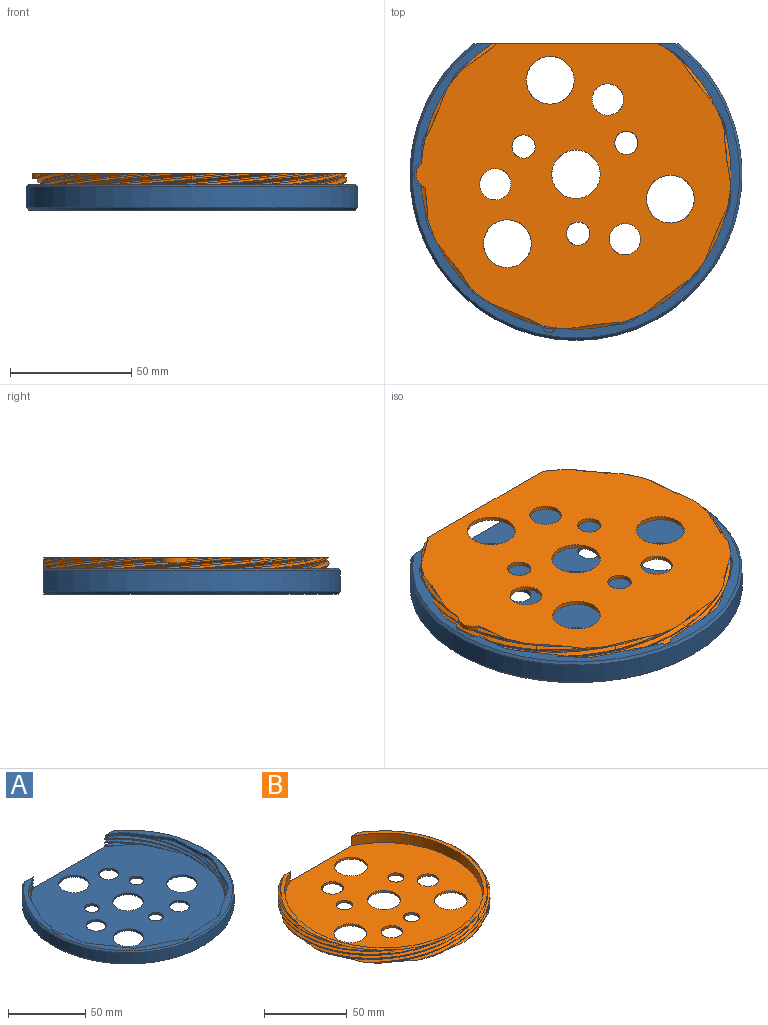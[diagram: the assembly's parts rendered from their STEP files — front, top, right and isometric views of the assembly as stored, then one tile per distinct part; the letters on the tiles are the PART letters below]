
ASSEMBLY  parts=2 mates=1
PART A: 110 faces, bbox 137.5x125.1x13.2 mm
  f0: cylinder r=63.1mm len=7.96mm, axis (0,0,1), area 4.3mm2, adj f1,f2,f33,f59
  f1: plane 128.57x118.32mm, normal (0,0,1), area 10495.3mm2, adj f0,f2,f3,f12,f13,f14,f15,f16
  f2: plane 84.9x10.88mm, normal (0,1,0), area 288.5mm2, adj f0,f1,f4,f5,f6,f7,f8,f9
  f3: cylinder r=10mm len=20mm, axis (0,0,-1), area 100.5mm2, adj f1,f5
  f4: cylinder r=68.6mm len=137.2mm, axis (0,0,-1), area 2922.7mm2, adj f2,f95,f96
  f5: plane 135.2x121.6mm, normal (0,0,-1), area 11755.3mm2, adj f2,f3,f95,f101,f102,f103,f104,f105
  f6: bspline ~56.05x33.17mm, area 111.1mm2, adj f2,f8,f61,f88,f98
  f7: bspline ~56.05x33.17mm, area 83.7mm2, adj f2,f8,f60,f90
  f8: bspline ~56.17x32.5mm, area 22.3mm2, adj f2,f6,f7,f89
  f9: bspline ~56.05x33.17mm, area 48.2mm2, adj f2,f11,f60,f91
  f10: bspline ~24.5x24.5mm, area 20.8mm2, adj f2,f11,f58,f93
  f11: bspline ~23.81x23.81mm, area 7.5mm2, adj f2,f9,f10,f92
  f12: bspline ~88.41x33.17mm, area 146.2mm2, adj f1,f14,f62,f63,f84
  f13: bspline ~88.41x33.17mm, area 146.8mm2, adj f1,f14,f42,f82
  f14: bspline ~88.6x32.5mm, area 34.4mm2, adj f1,f12,f13,f83
  f15: bspline ~88.41x33.17mm, area 144.9mm2, adj f1,f2,f17,f61,f87
  f16: bspline ~88.41x33.17mm, area 146.8mm2, adj f1,f17,f62,f85
  f17: bspline ~88.6x32.5mm, area 34.4mm2, adj f1,f15,f16,f86
  f18: bspline ~88.41x33.17mm, area 146.2mm2, adj f1,f20,f46,f47,f75
  f19: bspline ~88.41x33.17mm, area 146.8mm2, adj f1,f20,f48,f73
  f20: bspline ~88.6x32.5mm, area 34.4mm2, adj f1,f18,f19,f74
  f21: bspline ~64.72x64.72mm, area 146.2mm2, adj f1,f23,f48,f49,f72
  f22: bspline ~64.72x64.72mm, area 146.8mm2, adj f1,f23,f50,f70
  f23: bspline ~64.86x64.86mm, area 34.4mm2, adj f1,f21,f22,f71
  f24: bspline ~64.72x64.72mm, area 146.2mm2, adj f1,f26,f42,f43,f81
  f25: bspline ~64.72x64.72mm, area 146.8mm2, adj f1,f26,f44,f79,f100
  f26: bspline ~64.86x64.86mm, area 34.4mm2, adj f1,f24,f25,f80,f100
  f27: bspline ~74.82x33.17mm, area 146.2mm2, adj f1,f29,f44,f45,f78
  f28: bspline ~88.41x33.17mm, area 146.8mm2, adj f1,f29,f46,f76
  f29: bspline ~88.6x32.5mm, area 34.4mm2, adj f1,f27,f28,f77
  f30: bspline ~56.05x33.17mm, area 89mm2, adj f1,f2,f32,f56
  f31: bspline ~56.05x33.17mm, area 115.7mm2, adj f1,f2,f32,f54,f55
  f32: bspline ~56.17x32.5mm, area 23.5mm2, adj f1,f2,f30,f31
  f33: bspline ~24.5x24.5mm, area 26mm2, adj f0,f1,f2,f35
  f34: bspline ~23.84x23.41mm, area 52.7mm2, adj f1,f2,f35,f56,f57
  f35: bspline ~23.81x23.81mm, area 8.7mm2, adj f1,f2,f33,f34
  f36: bspline ~74.82x33.17mm, area 146.2mm2, adj f1,f38,f50,f51,f69
  f37: bspline ~88.41x33.17mm, area 146.8mm2, adj f1,f38,f52,f67
  f38: bspline ~88.6x32.5mm, area 34.4mm2, adj f1,f36,f37,f68
  f39: bspline ~88.41x33.17mm, area 146.2mm2, adj f1,f41,f52,f53,f66
  f40: bspline ~88.41x33.17mm, area 146.6mm2, adj f1,f2,f41,f54,f64
  f41: bspline ~88.6x32.5mm, area 34.4mm2, adj f1,f39,f40,f65
  f42: cylinder r=63.1mm len=69.34mm, axis (0,0,1), area 75mm2, adj f1,f13,f24,f43,f81,f82,f94
  f43: bspline ~10.54x2.52mm, area 0.5mm2, adj f1,f24,f42
  f44: cylinder r=63.1mm len=67.62mm, axis (0,0,1), area 75mm2, adj f1,f25,f27,f45,f78,f79,f94
  f45: bspline ~10.16x5.89mm, area 0.5mm2, adj f1,f27,f44
  f46: cylinder r=63.1mm len=79.07mm, axis (0,0,1), area 75mm2, adj f1,f18,f28,f47,f75,f76,f94
  f47: bspline ~9.49x7.32mm, area 0.5mm2, adj f1,f18,f46
  f48: cylinder r=63.1mm len=69.34mm, axis (0,0,1), area 75mm2, adj f1,f19,f21,f49,f72,f73,f94
  f49: bspline ~10.54x2.52mm, area 0.5mm2, adj f1,f21,f48
  f50: cylinder r=63.1mm len=67.62mm, axis (0,0,1), area 75mm2, adj f1,f22,f36,f51,f69,f70,f94
  f51: bspline ~10.16x5.89mm, area 0.5mm2, adj f1,f36,f50
  f52: cylinder r=63.1mm len=79.07mm, axis (0,0,1), area 75mm2, adj f1,f37,f39,f53,f66,f67,f94
  f53: bspline ~9.49x7.32mm, area 0.5mm2, adj f1,f39,f52
  f54: cylinder r=63.1mm len=65.01mm, axis (0,0,1), area 54.1mm2, adj f1,f2,f31,f40,f55
  f55: bspline ~10.54x2.52mm, area 0.5mm2, adj f1,f31,f54
  f56: cylinder r=63.1mm len=32.47mm, axis (0,0,1), area 29.2mm2, adj f1,f2,f30,f34,f57
  f57: bspline ~10.16x5.89mm, area 0.5mm2, adj f1,f34,f56
  f58: cylinder r=63.1mm len=5.83mm, axis (0,0,1), area 16.4mm2, adj f2,f10,f93,f94
  f59: bspline ~9.49x7.32mm, area 0.1mm2, adj f0,f1,f2
  f60: cylinder r=63.1mm len=29.92mm, axis (0,0,1), area 43.7mm2, adj f2,f7,f9,f90,f91,f94
  f61: cylinder r=63.1mm len=62.31mm, axis (0,0,1), area 55.7mm2, adj f2,f6,f15,f87,f94,f97,f98
  f62: cylinder r=63.1mm len=79.07mm, axis (0,0,1), area 75mm2, adj f1,f12,f16,f63,f84,f85,f94
  f63: bspline ~9.49x7.32mm, area 0.5mm2, adj f1,f12,f62
  f64: extruded ~7.96x4.01mm, area 17.8mm2, adj f2,f40,f65,f94
  f65: extruded ~3.15x2.77mm, area 8.4mm2, adj f41,f64,f66,f94
  f66: extruded ~8.75x5.76mm, area 21mm2, adj f39,f52,f65,f94
  f67: extruded ~8.81x5.95mm, area 21.3mm2, adj f37,f52,f68,f94
  f68: extruded ~3.98x2mm, area 8.4mm2, adj f38,f67,f69,f94
  f69: extruded ~10.46x2mm, area 21mm2, adj f36,f50,f68,f94
  f70: extruded ~10.61x2mm, area 21.3mm2, adj f22,f50,f71,f94
  f71: extruded ~4.12x2mm, area 8.4mm2, adj f23,f70,f72,f94
  f72: extruded ~9.36x4.7mm, area 21mm2, adj f21,f48,f71,f94
  f73: extruded ~9.56x4.65mm, area 21.3mm2, adj f19,f48,f74,f94
  f74: extruded ~3.15x2.77mm, area 8.4mm2, adj f20,f73,f75,f94
  f75: extruded ~8.75x5.76mm, area 21mm2, adj f18,f46,f74,f94
  f76: extruded ~8.81x5.95mm, area 21.3mm2, adj f28,f46,f77,f94
  f77: extruded ~3.98x2mm, area 8.4mm2, adj f29,f76,f78,f94
  f78: extruded ~10.46x2mm, area 21mm2, adj f27,f44,f77,f94
  f79: extruded ~8.75x2mm, area 17.6mm2, adj f25,f44,f94,f99
  f80: extruded ~2x1.13mm, area 2.4mm2, adj f26,f81,f94,f99
  f81: extruded ~9.36x4.7mm, area 21mm2, adj f24,f42,f80,f94
  f82: extruded ~9.56x4.65mm, area 21.3mm2, adj f13,f42,f83,f94
  f83: extruded ~3.15x2.77mm, area 8.4mm2, adj f14,f82,f84,f94
  f84: extruded ~8.75x5.76mm, area 21mm2, adj f12,f62,f83,f94
  f85: extruded ~8.81x5.95mm, area 21.3mm2, adj f16,f62,f86,f94
  f86: extruded ~3.98x2mm, area 8.4mm2, adj f17,f85,f87,f94
  f87: extruded ~10.46x2mm, area 21mm2, adj f15,f61,f86,f94
  f88: extruded ~4.68x2mm, area 9.4mm2, adj f6,f89,f94,f97
  f89: extruded ~4.12x2mm, area 8.4mm2, adj f8,f88,f90,f94
  f90: extruded ~9.36x4.7mm, area 21mm2, adj f7,f60,f89,f94
  f91: extruded ~9.56x4.65mm, area 21.3mm2, adj f9,f60,f92,f94
  f92: extruded ~3.15x2.77mm, area 8.4mm2, adj f11,f91,f93,f94
  f93: extruded ~8.75x5.76mm, area 21mm2, adj f10,f58,f92,f94
  f94: plane 135.29x121.69mm, normal (0,0,1), area 1215.9mm2, adj f2,f42,f44,f46,f48,f50,f52,f58
  f95: cone r=68.6mm half-angle=45deg, axis (0,0,1), area 478.9mm2, adj f2,f4,f5
  f96: cone r=67.6mm half-angle=45deg, axis (0,0,-1), area 478.9mm2, adj f2,f4,f94
  f97: cylinder r=7mm len=12.35mm, axis (0,0,1), area 30.4mm2, adj f61,f88,f94,f98
  f98: plane 12.38x4.26mm, normal (0,0,1), area 33.4mm2, adj f6,f61,f97
  f99: cylinder r=2.5mm len=4.84mm, axis (0,0,1), area 13.4mm2, adj f79,f80,f94,f100
  f100: plane 4.99x2.32mm, normal (0,0,1), area 6.3mm2, adj f25,f26,f99
  f101: cylinder r=4.81mm len=9.61mm, axis (0,0,-1), area 48.3mm2, adj f1,f5
  f102: cylinder r=9.88mm len=19.75mm, axis (0,0,-1), area 99.3mm2, adj f1,f5
  f103: cylinder r=6.48mm len=12.97mm, axis (0,0,-1), area 65.2mm2, adj f1,f5
  f104: cylinder r=4.81mm len=9.61mm, axis (0,0,-1), area 48.3mm2, adj f1,f5
  f105: cylinder r=9.88mm len=19.75mm, axis (0,0,-1), area 99.3mm2, adj f1,f5
  f106: cylinder r=6.48mm len=12.97mm, axis (0,0,-1), area 65.2mm2, adj f1,f5
  f107: cylinder r=4.81mm len=9.61mm, axis (0,0,-1), area 48.3mm2, adj f1,f5
  f108: cylinder r=9.88mm len=19.75mm, axis (0,0,-1), area 99.3mm2, adj f1,f5
  f109: cylinder r=6.48mm len=12.97mm, axis (0,0,-1), area 65.2mm2, adj f1,f5
PART B: 109 faces, bbox 130.1x126.5x14.6 mm
  f0: bspline ~10.5x1.88mm, area 0.4mm2, adj f1,f76,f98
  f1: cylinder r=64mm len=77.53mm, axis (0,0,-1), area 36.1mm2, adj f0,f16,f65,f76,f78,f87,f98,f99
  f2: cylinder r=64mm len=75.65mm, axis (0,0,-1), area 36.5mm2, adj f16,f62,f66,f69,f88
  f3: cylinder r=64mm len=75.65mm, axis (0,0,-1), area 36.5mm2, adj f16,f35,f39,f56,f91
  f4: cylinder r=64mm len=58.63mm, axis (0,0,-1), area 36.5mm2, adj f16,f50,f53,f57,f90
  f5: cylinder r=64mm len=58.63mm, axis (0,0,-1), area 36.5mm2, adj f16,f44,f59,f63,f89
  f6: cylinder r=64mm len=77.53mm, axis (0,0,-1), area 36.5mm2, adj f16,f38,f41,f45,f93
  f7: cylinder r=64mm len=75.65mm, axis (0,0,-1), area 36.5mm2, adj f16,f25,f29,f32,f95
  f8: cylinder r=64mm len=77.53mm, axis (0,0,-1), area 36.5mm2, adj f16,f28,f47,f51,f92
  f9: cylinder r=64mm len=15.18mm, axis (0,0,-1), area 6.8mm2, adj f15,f20,f24,f96
  f10: cylinder r=64mm len=43.66mm, axis (0,0,-1), area 19.4mm2, adj f15,f19,f33,f94
  f11: cylinder r=64mm len=18.67mm, axis (0,0,-1), area 15.1mm2, adj f15,f16,f73,f81
  f12: cylinder r=64mm len=49.38mm, axis (0,0,-1), area 27.8mm2, adj f15,f16,f75,f82,f84,f99
  f13: plane 120x114mm, normal (0,0,1), area 9250.9mm2, adj f14,f15,f17,f100,f101,f102,f103,f104
  f14: cylinder r=10mm len=20mm, axis (0,0,-1), area 100.5mm2, adj f13,f16
  f15: plane 68.75x8.65mm, normal (0,1,0), area 190.4mm2, adj f9,f10,f11,f12,f13,f16,f17,f18
  f16: plane 129.9x117.9mm, normal (0,0,-1), area 10370.3mm2, adj f1,f2,f3,f4,f5,f6,f7,f8
  f17: cylinder r=60mm len=120mm, axis (0,0,-1), area 2260.1mm2, adj f13,f15,f18
  f18: plane 125.06x116.56mm, normal (0,0,1), area 791.7mm2, adj f15,f17,f19,f20,f21,f22,f23,f24
  f19: bspline ~55.43x32.81mm, area 99.6mm2, adj f10,f15,f18,f21,f94
  f20: bspline ~55.43x32.81mm, area 64.5mm2, adj f9,f15,f18,f21,f96
  f21: bspline ~62.38x62.38mm, area 43mm2, adj f15,f18,f19,f20
  f22: bspline ~54.02x31.3mm, area 15.5mm2, adj f15,f18,f23,f24
  f23: bspline ~24.24x24.24mm, area 7.9mm2, adj f15,f18,f22,f97
  f24: bspline ~24.24x24.24mm, area 37.4mm2, adj f9,f15,f18,f22,f96
  f25: bspline ~25.28x22.34mm, area 24.3mm2, adj f7,f16,f27,f29
  f26: bspline ~25.28x22.34mm, area 3.2mm2, adj f16,f27,f28
  f27: bspline ~23.99x21.05mm, area 8.4mm2, adj f16,f25,f26,f30
  f28: bspline ~81.93x24.95mm, area 162.6mm2, adj f8,f16,f18,f26,f30,f92
  f29: bspline ~75.77x18.47mm, area 129.4mm2, adj f7,f18,f25,f30,f95
  f30: bspline ~79.37x22.84mm, area 70.3mm2, adj f18,f27,f28,f29
  f31: bspline ~0.73x0.26mm, area 0.1mm2, adj f15,f34
  f32: bspline ~87.43x32.81mm, area 161.4mm2, adj f7,f15,f16,f18,f34,f95
  f33: bspline ~87.43x32.81mm, area 126.8mm2, adj f10,f15,f18,f34,f94
  f34: bspline ~85.21x31.3mm, area 70.3mm2, adj f15,f18,f31,f32,f33
  f35: bspline ~25.28x22.34mm, area 24.3mm2, adj f3,f16,f37,f39
  f36: bspline ~25.28x22.34mm, area 3.2mm2, adj f16,f37,f38
  f37: bspline ~23.99x21.05mm, area 8.4mm2, adj f16,f35,f36,f40
  f38: bspline ~81.93x24.95mm, area 162.6mm2, adj f6,f16,f18,f36,f40,f93
  f39: bspline ~75.77x18.47mm, area 129.4mm2, adj f3,f18,f35,f40,f91
  f40: bspline ~79.37x22.84mm, area 70.3mm2, adj f18,f37,f38,f39
  f41: bspline ~31.93x7.88mm, area 24.3mm2, adj f6,f16,f43,f45
  f42: bspline ~31.94x7.88mm, area 3.2mm2, adj f16,f43,f44
  f43: bspline ~31.14x6.46mm, area 8.4mm2, adj f16,f41,f42,f46
  f44: bspline ~64x64mm, area 162.6mm2, adj f5,f16,f18,f42,f46,f89
  f45: bspline ~64x64mm, area 129.4mm2, adj f6,f18,f41,f46,f93
  f46: bspline ~62.38x62.38mm, area 70.3mm2, adj f18,f43,f44,f45
  f47: bspline ~31.93x7.88mm, area 24.3mm2, adj f8,f16,f49,f51
  f48: bspline ~31.94x7.88mm, area 3.2mm2, adj f16,f49,f50
  f49: bspline ~31.14x6.46mm, area 8.4mm2, adj f16,f47,f48,f52
  f50: bspline ~64x64mm, area 162.6mm2, adj f4,f16,f18,f48,f52,f90
  f51: bspline ~64x64mm, area 129.4mm2, adj f8,f18,f47,f52,f92
  f52: bspline ~62.38x62.38mm, area 70.3mm2, adj f18,f49,f50,f51
  f53: bspline ~18.07x9.25mm, area 24.3mm2, adj f4,f16,f55,f57
  f54: bspline ~5.55x3.77mm, area 3.2mm2, adj f16,f55,f56
  f55: bspline ~12.68x6.34mm, area 8.4mm2, adj f16,f53,f54,f58
  f56: bspline ~87.43x32.81mm, area 162.6mm2, adj f3,f16,f18,f54,f58,f91
  f57: bspline ~87.43x32.81mm, area 129.4mm2, adj f4,f18,f53,f58,f90
  f58: bspline ~85.21x31.3mm, area 70.3mm2, adj f18,f55,f56,f57
  f59: bspline ~18.07x9.25mm, area 24.3mm2, adj f5,f16,f61,f63
  f60: bspline ~5.55x3.77mm, area 3.2mm2, adj f16,f61,f62
  f61: bspline ~12.68x6.34mm, area 8.4mm2, adj f16,f59,f60,f64
  f62: bspline ~87.43x32.81mm, area 162.6mm2, adj f2,f16,f18,f60,f64,f88
  f63: bspline ~87.43x32.81mm, area 129.4mm2, adj f5,f18,f59,f64,f89
  f64: bspline ~85.21x31.3mm, area 70.3mm2, adj f18,f61,f62,f63
  f65: bspline ~81.93x24.95mm, area 162.6mm2, adj f1,f16,f18,f67,f70,f87
  f66: bspline ~25.28x22.34mm, area 24.3mm2, adj f2,f16,f68,f69
  f67: bspline ~25.28x22.34mm, area 3.2mm2, adj f16,f65,f68
  f68: bspline ~23.99x21.05mm, area 8.4mm2, adj f16,f66,f67,f70
  f69: bspline ~75.77x18.47mm, area 129.4mm2, adj f2,f18,f66,f70,f88
  f70: bspline ~79.37x22.84mm, area 70.3mm2, adj f18,f65,f68,f69
  f71: bspline ~25.28x22.34mm, area 2.4mm2, adj f15,f16,f72
  f72: bspline ~23.99x21.05mm, area 8.4mm2, adj f15,f16,f71,f73,f74
  f73: bspline ~25.28x22.34mm, area 21.7mm2, adj f11,f15,f16,f72
  f74: bspline ~0.73x0.28mm, area 0.1mm2, adj f15,f72
  f75: bspline ~55.43x32.81mm, area 112.2mm2, adj f12,f15,f77,f99
  f76: bspline ~55.43x32.81mm, area 114.4mm2, adj f0,f1,f15,f77,f87,f98,f99
  f77: bspline ~62.38x62.38mm, area 50.3mm2, adj f15,f75,f76,f99
  f78: bspline ~29.89x7.88mm, area 15.4mm2, adj f1,f16,f80,f99
  f79: bspline ~29.9x7.88mm, area 0mm2, adj f16,f80,f99
  f80: bspline ~29.11x6.46mm, area 3.8mm2, adj f16,f78,f79,f99
  f81: bspline ~24.24x24.24mm, area 57.8mm2, adj f11,f15,f16,f83,f85
  f82: bspline ~24.24x24.24mm, area 59.6mm2, adj f12,f15,f83,f84
  f83: bspline ~54.02x31.3mm, area 27.5mm2, adj f15,f81,f82,f86
  f84: bspline ~18.07x9.25mm, area 24.3mm2, adj f12,f16,f82,f86
  f85: bspline ~5.55x3.77mm, area 3.2mm2, adj f16,f81,f86
  f86: bspline ~12.68x6.34mm, area 8.4mm2, adj f16,f83,f84,f85
  f87: cone r=64mm half-angle=49.1deg, axis (0,0,-1), area 18.2mm2, adj f1,f15,f18,f65,f76
  f88: cone r=64mm half-angle=49.1deg, axis (0,0,-1), area 27.2mm2, adj f2,f18,f62,f69
  f89: cone r=64mm half-angle=49.1deg, axis (0,0,-1), area 27.2mm2, adj f5,f18,f44,f63
  f90: cone r=64mm half-angle=49.1deg, axis (0,0,-1), area 27.2mm2, adj f4,f18,f50,f57
  f91: cone r=64mm half-angle=49.1deg, axis (0,0,-1), area 27.2mm2, adj f3,f18,f39,f56
  f92: cone r=64mm half-angle=49.1deg, axis (0,0,-1), area 27.2mm2, adj f8,f18,f28,f51
  f93: cone r=64mm half-angle=49.1deg, axis (0,0,-1), area 27.2mm2, adj f6,f18,f38,f45
  f94: cone r=64mm half-angle=49.1deg, axis (0,0,-1), area 27.2mm2, adj f10,f18,f19,f33
  f95: cone r=64mm half-angle=49.1deg, axis (0,0,-1), area 27.2mm2, adj f7,f18,f29,f32
  f96: cone r=64mm half-angle=49.1deg, axis (0,0,-1), area 27.2mm2, adj f9,f18,f20,f24
  f97: cone r=64mm half-angle=49.1deg, axis (0,0,-1), area 6.8mm2, adj f15,f18,f23
  f98: plane 10.07x3.49mm, normal (0,0,1), area 17.2mm2, adj f0,f1,f76,f99
  f99: cylinder r=6mm len=11.25mm, axis (0,0,-1), area 26.3mm2, adj f1,f12,f16,f75,f76,f77,f78,f79
  f100: cylinder r=4.81mm len=9.61mm, axis (0,0,-1), area 48.3mm2, adj f13,f16
  f101: cylinder r=4.81mm len=9.61mm, axis (0,0,-1), area 48.3mm2, adj f13,f16
  f102: cylinder r=6.48mm len=12.97mm, axis (0,0,-1), area 65.2mm2, adj f13,f16
  f103: cylinder r=9.88mm len=19.75mm, axis (0,0,-1), area 99.3mm2, adj f13,f16
  f104: cylinder r=4.81mm len=9.61mm, axis (0,0,-1), area 48.3mm2, adj f13,f16
  f105: cylinder r=6.48mm len=12.97mm, axis (0,0,-1), area 65.2mm2, adj f13,f16
  f106: cylinder r=9.88mm len=19.75mm, axis (0,0,-1), area 99.3mm2, adj f13,f16
  f107: cylinder r=9.88mm len=19.75mm, axis (0,0,-1), area 99.3mm2, adj f13,f16
  f108: cylinder r=6.48mm len=12.97mm, axis (0,0,-1), area 65.2mm2, adj f13,f16
PLACE A t=(-90,0,0)mm
PLACE B rot(axis=(0,1,0),180deg) t=(-90,0,14.9)mm
MATE cylindrical A.f3 <-> B.f17  axis (0,0,-1) through (0,0,1.6)mm
